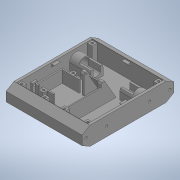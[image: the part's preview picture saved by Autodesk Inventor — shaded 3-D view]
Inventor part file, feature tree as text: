
AUTODESK INVENTOR PART (.ipt)
format: ipt  version: 2020 (Build 240168000, 168)  size: 701,440 bytes
history: native  units: in
note: dims shown in document units (in); Inventor stores cm internally (conversion verified against a paired STEP export)
features: extrude x21, sketch x21, projected_geometry x16, mirror x7, plane x1
ambient origin geometry x8: Origin, YZ Plane, XZ Plane, XY Plane, X Axis, Y Axis, Z Axis, Center Point
bodies: Solid1 (feature_tree)
feature tree (66):
  extrude  "Extrusion1"  Depth=5.9055in
  extrude  "Extrusion2"  TaperAngle=0.0deg  [1 undecoded]
  extrude  "Extrusion3"  Depth=1.063in
  extrude  "Extrusion4"  Depth=0.315in
  extrude  "Extrusion5"  TaperAngle=0.0deg  [1 undecoded]
  extrude  "Extrusion6"  Depth=0.5906in
  mirror  "Mirror1"
  extrude  "Extrusion7"  Depth=0.0787in
  mirror  "Mirror2"
  extrude  "Extrusion8"  Depth=0.6102in
  mirror  "Mirror3"
  plane  "Work Plane1"
  extrude  "Extrusion9"  Depth=0.7874in TaperAngle=0.0deg
  mirror  "Mirror4"
  extrude  "Extrusion10"  Depth=6.063in TaperAngle=0.0deg
  extrude  "Extrusion11"  Depth=0.1575in
  extrude  "Extrusion12"  TaperAngle=0.0deg  [1 undecoded]
  extrude  "Extrusion13"  Depth=0.2756in
  extrude  "Extrusion14"  Depth=0.4331in
  extrude  "Extrusion17"  Depth=2.7559in
  extrude  "Extrusion18"  Depth=0.0453in
  mirror  "Mirror6"
  extrude  "Extrusion19"  TaperAngle=0.0deg  [1 undecoded]
  mirror  "Mirror7"
  extrude  "Extrusion20"  Depth=0.0787in
  extrude  "Extrusion21"  Depth=0.993in
  extrude  "Extrusion22"  Depth=0.2756in
  extrude  "Extrusion23"  Depth=0.4724in
  mirror  "Mirror8"
  sketch  "Sketch1"  dims[d0=1.1811in d1=5.9055in]
  sketch  "Sketch2"  dims[d2=4.8819in d3=0.0in]
  projected_geometry  "Projected Loop1"
  sketch  "Sketch3"  dims[d4=0.1575in d5=1.063in]
  projected_geometry  "Projected Loop2"
  projected_geometry  "Projected Loop3"
  sketch  "Sketch4"  dims[d6=0.0in d8=0.315in]
  sketch  "Sketch5"  dims[d10=0.993in d11=0.0in]
  projected_geometry  "Projected Loop4"
  sketch  "Sketch6"  dims[d12=0.6496in d13=0.5906in]
  sketch  "Sketch7"  dims[d14=1.5748in d15=0.0787in]
  sketch  "Sketch9"  dims[d16=0.5512in d17=0.0in d18=0.6102in]
  sketch  "Sketch10"  dims[d19=0.4803in d20=0.7874in d21=0.0in]
  sketch  "Sketch12"  dims[d22=0.1654in d23=6.063in d24=0.0in]
  projected_geometry  "Projected Loop6"
  projected_geometry  "Projected Loop7"
  projected_geometry  "Projected Loop8"
  sketch  "Sketch13"  dims[d25=0.5114in d26=0.1575in]
  sketch  "Sketch14"  dims[d27=1.5748in d28=0.0in d29=0.0in]
  sketch  "Sketch15"  dims[d30=0.1575in d31=0.2756in]
  projected_geometry  "Projected Loop15"
  sketch  "Sketch16"  dims[d32=0.0in d33=0.4331in]
  projected_geometry  "Projected Loop19"
  projected_geometry  "Projected Loop20"
  projected_geometry  "Projected Loop21"
  projected_geometry  "Projected Loop22"
  projected_geometry  "Projected Loop23"
  projected_geometry  "Projected Loop24"
  sketch  "Sketch20"  dims[d34=0.0906in d38=2.7559in]
  sketch  "Sketch21"  dims[d40=0.0453in d41=0.0909in]
  sketch  "Sketch22"  dims[d42=0.2362in d43=0.0in]
  sketch  "Sketch23"  dims[d44=60.0deg d45=0.0787in]
  sketch  "Sketch25"  dims[d46=0.315in d48=0.993in]
  sketch  "Sketch26"  dims[d49=0.0in d53=0.2756in]
  projected_geometry  "Projected Loop25"
  sketch  "Sketch27"  dims[d54=0.0in d55=0.4724in d56=1.1811in d57=1.5748in d58=1.5748in d59=0.0787in d60=0.0787in d62=0.315in d63=0.7677in d64=0.0in d66=0.1476in d67=0.2756in d68=0.0in d69=0.7874in d70=0.2953in d71=0.1181in d72=0.0in d89=0.0157in d90=0.0157in d91=0.1476in d92=0.1476in d96=0.315in d97=0.1575in d98=0.1181in d99=0.0in d102=0.1772in d104=0.3346in d105=135.0deg d106=0.2362in d107=0.0in d108=0.0394in d109=0.0in d110=0.063in d111=0.0394in d112=0.0in d117=0.993in d118=0.063in d119=0.3937in d120=0.0in d121=45.0deg d122=0.993in d123=0.1969in d124=0.3937in d125=0.0in d126=45.0deg d127=0.1969in d128=0.993in d129=0.3937in d130=0.0in]
  projected_geometry  "Projected Loop26"
note: 4 required parameter values undecoded (feature->parameter linkage not recoverable at this tier; creation-order binding heuristic only, values carry confidence <= 0.55)
